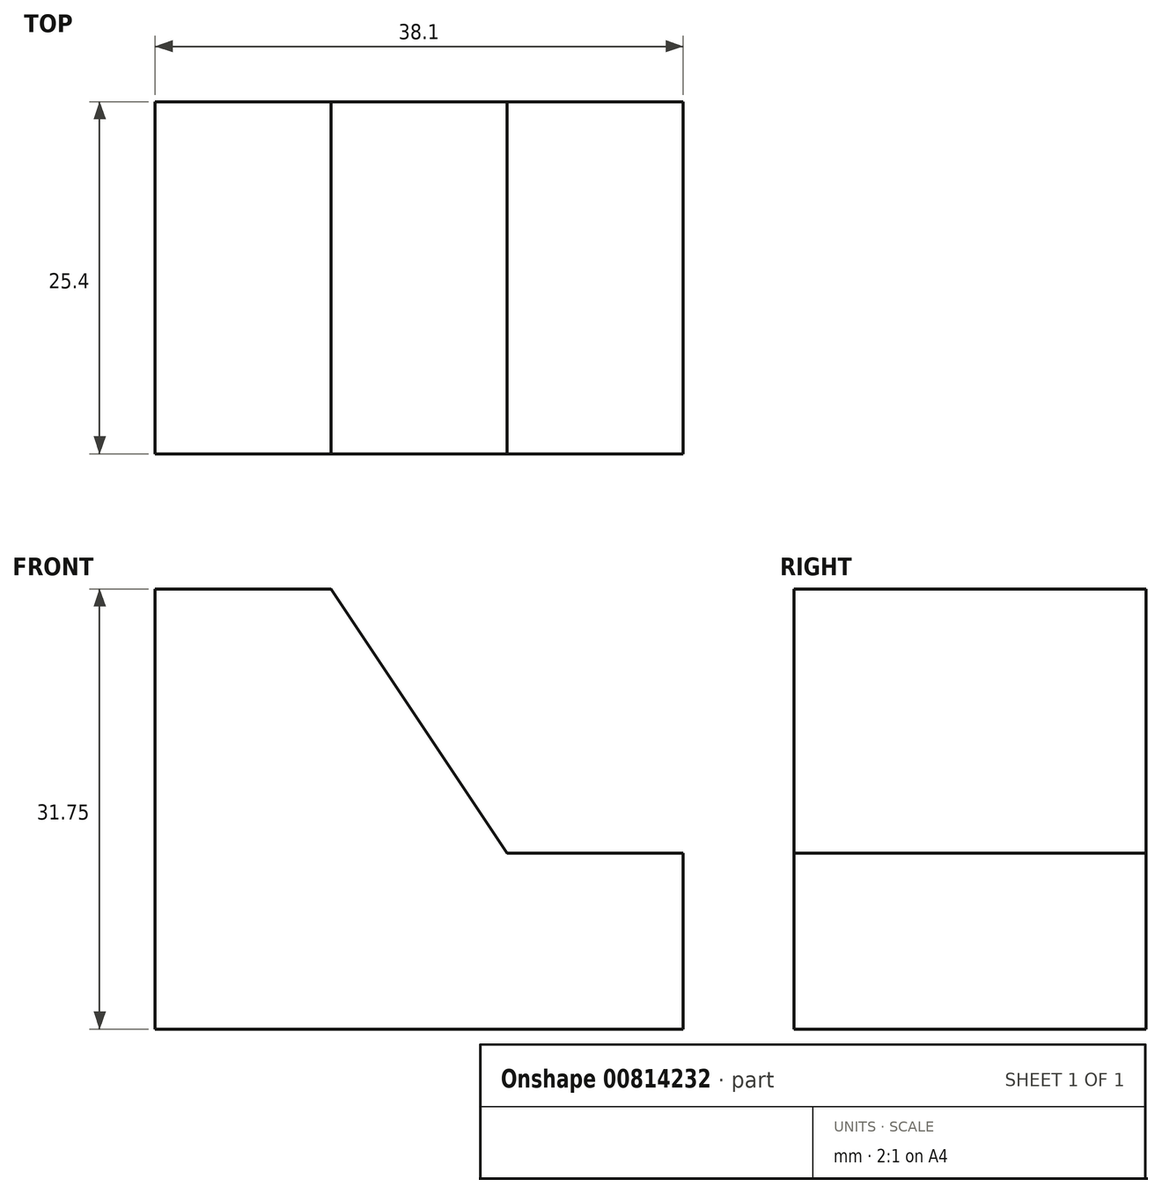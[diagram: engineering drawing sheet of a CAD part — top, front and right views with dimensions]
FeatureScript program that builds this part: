
annotation { "Feature Type Name" : "Feature", "Feature Type Description" : "" }
export const myFeature = defineFeature(function(context is Context, id is Id, definition is map)
    precondition{}
    {
        {
            var Q0;
            Q0=qCreatedBy(makeId("Front.planeOp"),FACE);
            var sketch = newSketch(context, id + "F0", { "sketchPlane" : qUnion([Q0])});
            skLineSegment(sketch, "E0.bottom", {"start": v(0, 0) * mm, "end": v(38.1, 0) * mm});
            skLineSegment(sketch, "E0.top", {"start": v(0, 31.75) * mm, "end": v(38.1, 31.75) * mm});
            skLineSegment(sketch, "E0.left", {"start": v(0, 0) * mm, "end": v(0, 31.75) * mm});
            skLineSegment(sketch, "E0.right", {"start": v(38.1, 0) * mm, "end": v(38.1, 31.75) * mm});
            skLineSegment(sketch, "E1", {"start": v(0, 31.75) * mm, "end": v(12.7, 31.75) * mm});
            skLineSegment(sketch, "E2", {"start": v(38.1, 0) * mm, "end": v(25.4, 0) * mm});
            skLineSegment(sketch, "E3", {"start": v(38.1, 0) * mm, "end": v(38.1, 12.7) * mm});
            skPoint(sketch, "E4.endSnap0", {"position": v(19.05, 31.75) * mm});
            skLineSegment(sketch, "E5", {"start": v(38.1, 12.7) * mm, "end": v(25.4, 12.7) * mm});
            skLineSegment(sketch, "E6", {"start": v(12.7, 31.75) * mm, "end": v(25.4, 12.7) * mm});
            skSolve(sketch);
        }
        {
            var Q0;
            Q0=makeQuery(id+"F0.imprint","IMPRINT",FACE,{"disambiguationData":[TD([[makeQuery(id+"F0.imprint","IMPRINT",EDGE,{"derivedFrom":sQuery(id+"F0.wireOp",EDGE,"E0.top")}),-1.0]])]});
            var Q1;
            Q1=makeQuery(id+"F0.imprint","IMPRINT",FACE,{"disambiguationData":[TD([[makeQuery(id+"F0.imprint","IMPRINT",EDGE,{"derivedFrom":sQuery(id+"F0.wireOp",EDGE,"E0.bottom")}),1.0]])]});
            var Q2;
            Q2 = qSketchRegion(id + "F2", true);
            extrude(context, id + "F1", {"entities" : qUnion([Q0, Q1, Q2]), "depth" : 25.4 * mm, "offsetDistance" : 25.4 * mm});
        }
        {
            var Q0;
            Q0=makeQuery(id+"F1.opExtrude","CAP_FACE",FACE,{"disambiguationData":[OSD([sQuery(id+"F0.wireOp",EDGE,"E0.bottom"),sQuery(id+"F0.wireOp",EDGE,"E0.top"),sQuery(id+"F0.wireOp",EDGE,"E0.left"),sQuery(id+"F0.wireOp",EDGE,"E0.right"),sQuery(id+"F0.wireOp",EDGE,"E1"),sQuery(id+"F0.wireOp",EDGE,"E2"),sQuery(id+"F0.wireOp",EDGE,"E3")])],"isStart":false});
            var sketch = newSketch(context, id + "F2", { "sketchPlane" : qUnion([Q0])});
            skSolve(sketch);
        }
        {
            var Q0;
            Q0=makeQuery(id+"F0.imprint","IMPRINT",FACE,{"disambiguationData":[TD([[makeQuery(id+"F0.imprint","IMPRINT",EDGE,{"derivedFrom":sQuery(id+"F0.wireOp",EDGE,"E0.top")}),-1.0]])]});
            extrude(context, id + "F3", {"entities" : qUnion([Q0]), "operationType" : NewBodyOperationType.REMOVE, "depth" : 25.4 * mm, "offsetDistance" : 25.4 * mm});
        }
    });
